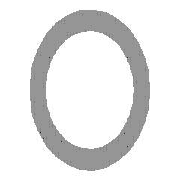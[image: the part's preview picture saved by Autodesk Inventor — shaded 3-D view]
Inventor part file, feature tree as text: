
AUTODESK INVENTOR PART (.ipt)
format: ipt  version: 2021 (Build 250183000, 183)  size: 316,928 bytes
history: native  units: mm (DEFAULTED — no unit token found)
features: other x13, plane x3, sketch x3, sweep x1, split x1
ambient origin geometry x8: Origin, YZ Plane, XZ Plane, XY Plane, X Axis, Y Axis, Z Axis, Center Point
bodies: Solid1 (feature_tree)
feature tree (21):
  parser-record x1  (decoder bookkeeping rows leaked as tree rows — omitted from the tree; the rows remain in map.json)
  other  "Driven Length"
  other  "Plano inicial"
  other  "Plano final"
  other  "Trayectoria de barrido"
  plane  "Plano de trabajo de orientación"
  sweep  "Cuerpo"
  plane  "Plano de trabajo11"
  split  "Dividir7"
  sketch  "Sketch3"  dims[d0=26.67mm d1=2.8702mm]
  plane  "Work Plane3"
  sketch  "Sketch4"  dims[d4=-0.0mm]
  sketch  "Boceto11"  dims[d5=506.111834mm d6=90.0deg d7=506.111834mm d8=0.0mm d9=0.0mm d226=0.0mm d227=90.0deg d228=0.0mm d229=90.0deg d230=5.0mm d231=0.0mm d232=5.0mm d233=0.0mm]
  other  "Sup151"
  other  "Sup153"
  other  "Sup154"
  other  "Sólido50"
  other  "SuperficieSolevación7"
  other  "Sup152"
  other  "Superficie de contorno97"
  other  "Superficie de contorno98"
